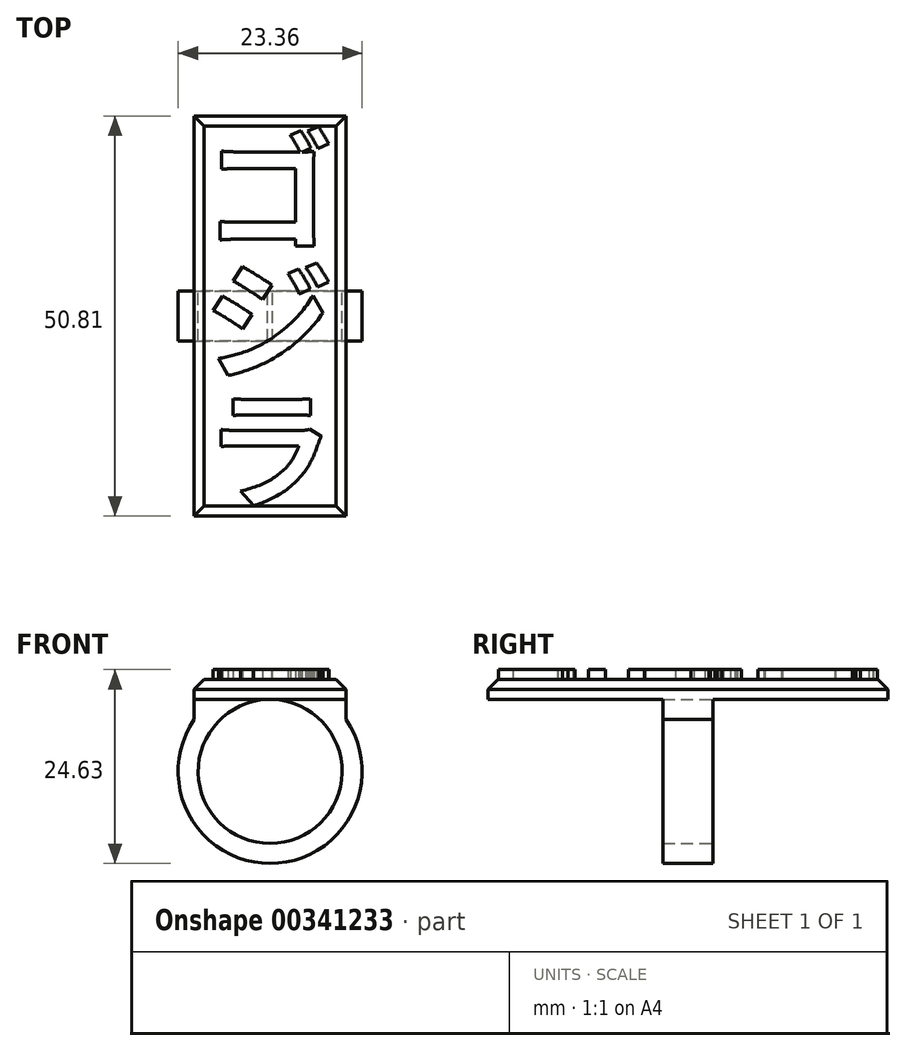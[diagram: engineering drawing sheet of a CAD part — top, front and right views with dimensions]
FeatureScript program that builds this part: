
annotation { "Feature Type Name" : "Feature", "Feature Type Description" : "" }
export const myFeature = defineFeature(function(context is Context, id is Id, definition is map)
    precondition{}
    {
        {
            var Q0;
            Q0=qCreatedBy(makeId("Front.planeOp"),FACE);
            var sketch = newSketch(context, id + "F0", { "sketchPlane" : qUnion([Q0])});
            skCircle(sketch, "E0", {"center": v(0, 0) * mm, "radius": 9.14 * mm});
            skLineSegment(sketch, "E1.left", {"start": v(-9.63, 6.61) * mm, "end": v(-9.63, 11.68) * mm});
            skLineSegment(sketch, "E1.right", {"start": v(9.63, 6.61) * mm, "end": v(9.63, 11.68) * mm});
            skPoint(sketch, "E1.middle", {"position": v(0, 9.14) * mm});
            skArc(sketch, "E2.trimOffspring", {"start": v(-9.63, 6.61) * mm, "mid": v(0, -11.68) * mm, "end": v(9.63, 6.61) * mm});
            skLineSegment(sketch, "E3", {"start": v(-9.63, 11.68) * mm, "end": v(9.63, 11.68) * mm});
            skSolve(sketch);
        }
        {
            var Q0;
            Q0 = qSketchRegion(id + "F0", true);
            extrude(context, id + "F1", {"entities" : qUnion([Q0]), "depth" : 6.35 * mm});
        }
        {
            var Q0;
            Q0=makeQuery(id+"F1.opExtrude","SWEPT_FACE",FACE,{"disambiguationData":[OSD([sQuery(id+"F0.wireOp",EDGE,"E3")])]});
            var sketch = newSketch(context, id + "F2", { "sketchPlane" : qUnion([Q0])});
            skLineSegment(sketch, "E4.bottom", {"start": v(-9.63, 22.22) * mm, "end": v(9.63, 22.22) * mm});
            skLineSegment(sketch, "E4.top", {"start": v(-9.63, -28.58) * mm, "end": v(9.63, -28.58) * mm});
            skLineSegment(sketch, "E4.left", {"start": v(-9.63, 22.22) * mm, "end": v(-9.63, -28.58) * mm});
            skLineSegment(sketch, "E4.right", {"start": v(9.63, 22.22) * mm, "end": v(9.63, -28.58) * mm});
            skPoint(sketch, "E4.middle", {"position": v(0, -3.18) * mm});
            skPoint(sketch, "E4.middle.positionSnap0", {"position": v(-9.63, -3.18) * mm});
            skPoint(sketch, "E4.cornerSnap0", {"position": v(-9.63, -3.18) * mm});
            skPoint(sketch, "E4.centerSnap0", {"position": v(-9.63, -3.18) * mm});
            skSolve(sketch);
        }
        {
            var Q0;
            Q0 = qSketchRegion(id + "F2", true);
            extrude(context, id + "F3", {"entities" : qUnion([Q0]), "operationType" : NewBodyOperationType.ADD, "oppositeDirection" : true, "depth" : 2.54 * mm});
        }
        {
            var Q0;
            Q0=makeQuery(id+"F3.boolean.opBoolean","MERGE",FACE,{"derivedFrom":[makeQuery(id+"F1.opExtrude","SWEPT_FACE",FACE,{"disambiguationData":[OSD([sQuery(id+"F0.wireOp",EDGE,"E3")])]}),makeQuery(id+"F3.opExtrude","CAP_FACE",FACE,{"disambiguationData":[OSD([sQuery(id+"F2.wireOp",EDGE,"E4.bottom"),sQuery(id+"F2.wireOp",EDGE,"E4.top"),sQuery(id+"F2.wireOp",EDGE,"E4.left"),sQuery(id+"F2.wireOp",EDGE,"E4.right")])],"isStart":true})]});
            var sketch = newSketch(context, id + "F4", { "sketchPlane" : qUnion([Q0])});
            skText(sketch, "E5", { "text": "ゴ\nジ\nラ", "fontName": "NotoSansCJKjp-Bold.otf"});
            const initialGuessF4  = {"E5": [-0.00838, 0.00662, 1, 0, 0.01185]};
            skSetInitialGuess(sketch, initialGuessF4);
            skSolve(sketch);
        }
        {
            var Q0;
            Q0 = qSketchRegion(id + "F4", true);
            extrude(context, id + "F5", {"entities" : qUnion([Q0]), "depth" : 1.27 * mm});
        }
        {
            var Q0;
            Q0=makeQuery(id+"F3.opExtrude","CAP_EDGE",EDGE,{"disambiguationData":[OSD([sQuery(id+"F2.wireOp",EDGE,"E4.bottom")])],"isStart":true});
            var Q1;
            Q1=makeQuery(id+"F3.boolean.opBoolean","MERGE",EDGE,{"derivedFrom":[makeQuery(id+"F1.opExtrude","SWEPT_EDGE",EDGE,{"disambiguationData":[OSD([sQuery(id+"F0.wireOp",EDGE,"E1.left"),sQuery(id+"F0.wireOp",EDGE,"E3")])]}),makeQuery(id+"F3.opExtrude","CAP_EDGE",EDGE,{"disambiguationData":[OSD([sQuery(id+"F2.wireOp",EDGE,"E4.left")])],"isStart":true})]});
            var Q2;
            Q2=makeQuery(id+"F3.boolean.opBoolean","MERGE",EDGE,{"derivedFrom":[makeQuery(id+"F1.opExtrude","SWEPT_EDGE",EDGE,{"disambiguationData":[OSD([sQuery(id+"F0.wireOp",EDGE,"E1.right"),sQuery(id+"F0.wireOp",EDGE,"E3")])]}),makeQuery(id+"F3.opExtrude","CAP_EDGE",EDGE,{"disambiguationData":[OSD([sQuery(id+"F2.wireOp",EDGE,"E4.right")])],"isStart":true})]});
            var Q3;
            Q3=makeQuery(id+"F3.opExtrude","CAP_EDGE",EDGE,{"disambiguationData":[OSD([sQuery(id+"F2.wireOp",EDGE,"E4.top")])],"isStart":true});
            chamfer(context, id + "F6", {"entities" : qUnion([Q0, Q1, Q2, Q3]), "width" : 1.27 * mm, "tangentPropagation" : true});
        }
    });
